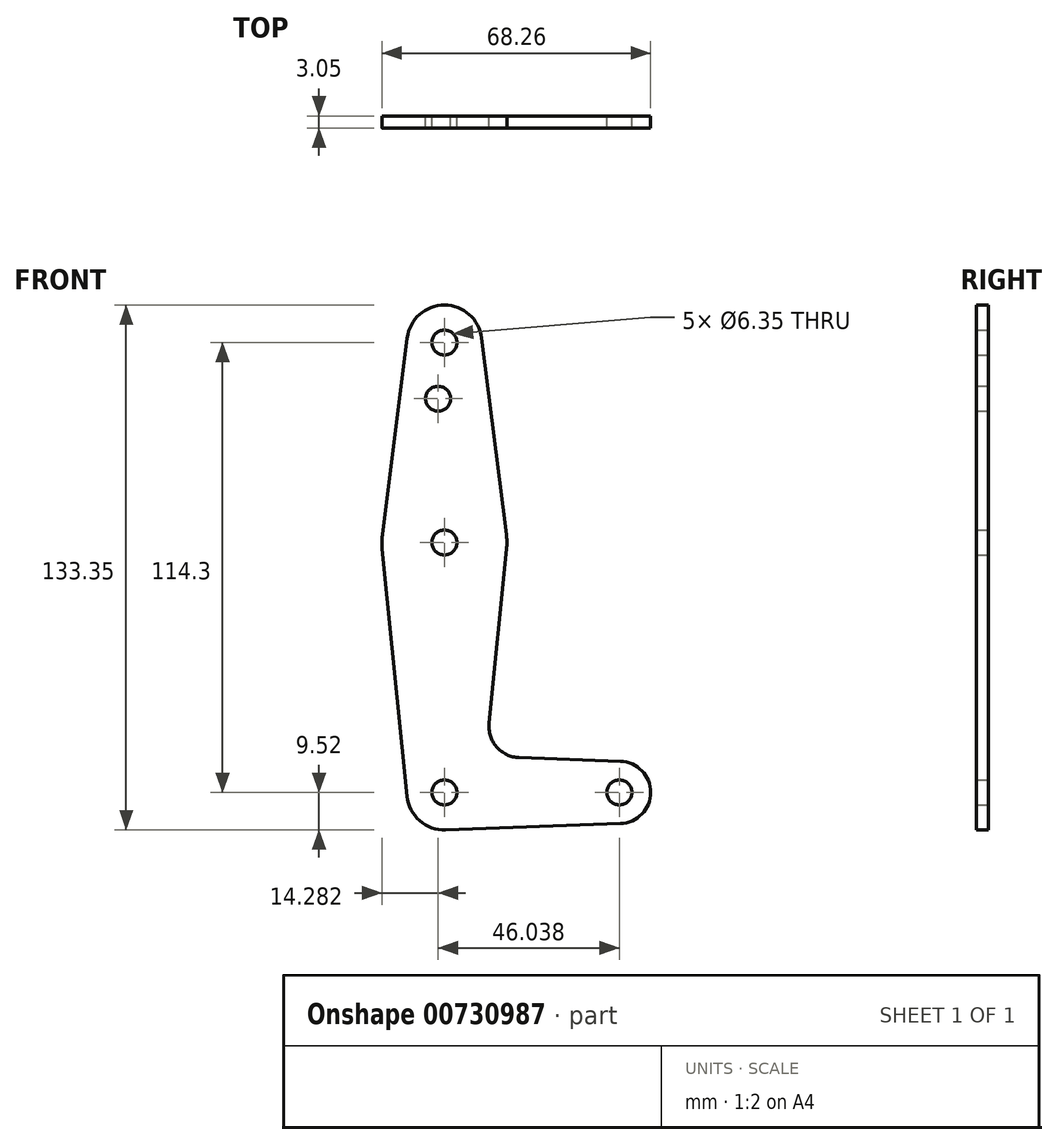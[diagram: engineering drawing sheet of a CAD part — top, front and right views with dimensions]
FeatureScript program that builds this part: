
annotation { "Feature Type Name" : "Feature", "Feature Type Description" : "" }
export const myFeature = defineFeature(function(context is Context, id is Id, definition is map)
    precondition{}
    {
        {
            var Q0;
            Q0=qCreatedBy(makeId("Front.planeOp"),FACE);
            var sketch = newSketch(context, id + "F0", { "sketchPlane" : qUnion([Q0])});
            skLineSegment(sketch, "E0", {"start": v(0, 0) * mm, "end": v(0, 114.3) * mm, "construction": true});
            skLineSegment(sketch, "E1", {"start": v(44.45, 0) * mm, "end": v(0, 0) * mm, "construction": true});
            skCircle(sketch, "E2", {"center": v(0, 0) * mm, "radius": 9.53 * mm});
            skCircle(sketch, "E3", {"center": v(0, 114.3) * mm, "radius": 9.53 * mm});
            skCircle(sketch, "E4", {"center": v(0, 63.5) * mm, "radius": 15.88 * mm});
            skCircle(sketch, "E5", {"center": v(44.45, 0) * mm, "radius": 7.94 * mm});
            skLineSegment(sketch, "E6", {"start": v(-9.45, 115.5) * mm, "end": v(-15.75, 65.48) * mm});
            skLineSegment(sketch, "E7", {"start": v(15.75, 65.48) * mm, "end": v(9.45, 115.5) * mm});
            skLineSegment(sketch, "E8", {"start": v(-15.8, 61.91) * mm, "end": v(-9.48, -0.95) * mm});
            skLineSegment(sketch, "E9", {"start": v(11.34, 17.6) * mm, "end": v(15.8, 61.91) * mm});
            skLineSegment(sketch, "E10", {"start": v(44.73, -7.93) * mm, "end": v(0.34, -9.52) * mm});
            skLineSegment(sketch, "E11", {"start": v(44.73, 7.93) * mm, "end": v(18.97, 8.85) * mm});
            skArc(sketch, "E12.filletArc", {"start": v(11.34, 17.6) * mm, "mid": v(13.26, 11.57) * mm, "end": v(18.97, 8.85) * mm});
            skCircle(sketch, "E13", {"center": v(-1.59, 100.03) * mm, "radius": 3.18 * mm});
            skCircle(sketch, "E14", {"center": v(0, 114.3) * mm, "radius": 3.18 * mm});
            skCircle(sketch, "E15", {"center": v(0, 0) * mm, "radius": 3.18 * mm});
            skCircle(sketch, "E16", {"center": v(44.45, 0) * mm, "radius": 3.18 * mm});
            skCircle(sketch, "E17", {"center": v(0, 63.5) * mm, "radius": 3.18 * mm});
            skSolve(sketch);
        }
        {
            var Q0;
            Q0 = qSketchRegion(id + "F0", true);
            extrude(context, id + "F1", {"entities" : qUnion([Q0]), "depth" : 3.05 * mm, "offsetDistance" : 25.4 * mm});
        }
    });
